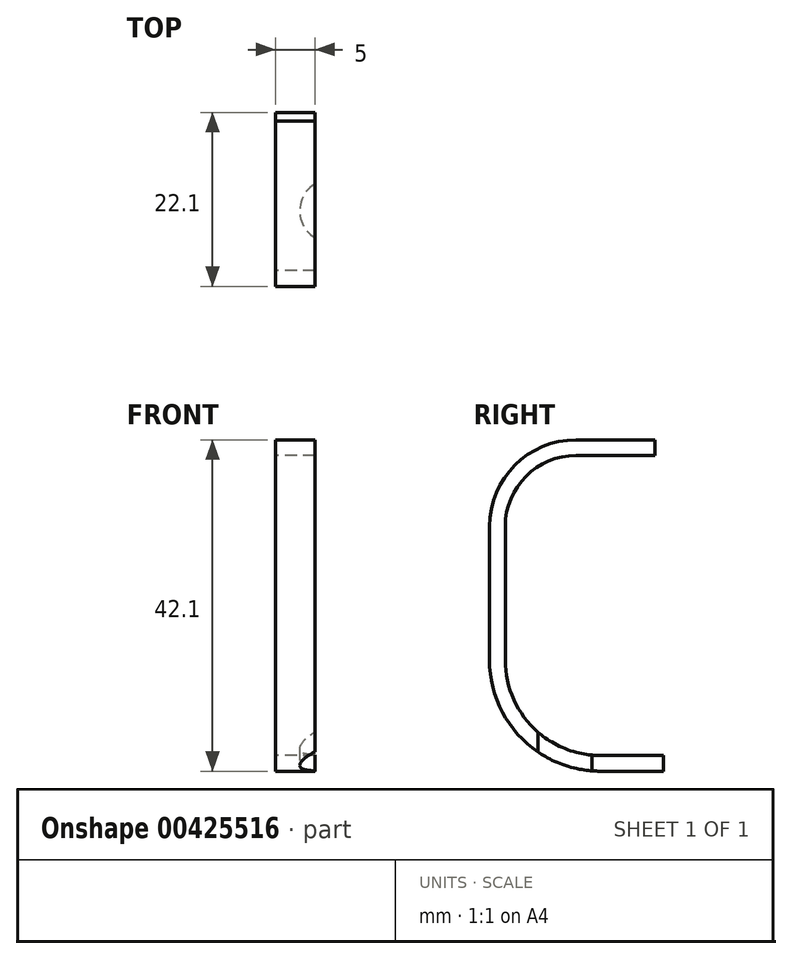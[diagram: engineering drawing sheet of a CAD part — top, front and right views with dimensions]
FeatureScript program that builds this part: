
annotation { "Feature Type Name" : "Feature", "Feature Type Description" : "" }
export const myFeature = defineFeature(function(context is Context, id is Id, definition is map)
    precondition{}
    {
        {
            var Q0;
            Q0=qCreatedBy(makeId("Right.planeOp"),FACE);
            var sketch = newSketch(context, id + "F0", { "sketchPlane" : qUnion([Q0])});
            skLineSegment(sketch, "E0", {"start": v(19, 9) * mm, "end": v(9, 9) * mm});
            skLineSegment(sketch, "E1", {"start": v(0, 0) * mm, "end": v(0, -17) * mm});
            skArc(sketch, "E2", {"start": v(9, 9) * mm, "mid": v(2.64, 6.36) * mm, "end": v(0, 0) * mm});
            skArc(sketch, "E3", {"start": v(0, -17) * mm, "mid": v(3.54, -25.56) * mm, "end": v(12.1, -29.1) * mm});
            skLineSegment(sketch, "E4.1", {"start": v(19, 11) * mm, "end": v(9, 11) * mm});
            skArc(sketch, "E4.2", {"start": v(9, 11) * mm, "mid": v(1.22, 7.78) * mm, "end": v(-2, 0) * mm});
            skLineSegment(sketch, "E4.3", {"start": v(-2, 0) * mm, "end": v(-2, -17) * mm});
            skArc(sketch, "E4.4", {"start": v(-2, -17) * mm, "mid": v(2.13, -26.97) * mm, "end": v(12.1, -31.1) * mm});
            skLineSegment(sketch, "E5", {"start": v(19, 11) * mm, "end": v(19, 9) * mm});
            skLineSegment(sketch, "E6", {"start": v(12.1, -29.1) * mm, "end": v(20.1, -29.1) * mm});
            skLineSegment(sketch, "E7", {"start": v(12.1, -31.1) * mm, "end": v(20.1, -31.1) * mm});
            skLineSegment(sketch, "E8", {"start": v(20.1, -29.1) * mm, "end": v(20.1, -31.1) * mm});
            skSolve(sketch);
        }
        {
            var Q0;
            Q0=makeQuery(id+"F0.imprint","IMPRINT",FACE,{"disambiguationData":[TD([[makeQuery(id+"F0.imprint","IMPRINT",EDGE,{"derivedFrom":sQuery(id+"F0.wireOp",EDGE,"E0")}),-1.0]])]});
            extrude(context, id + "F1", {"entities" : qUnion([Q0]), "depth" : 5 * mm});
        }
        {
            var Q0;
            Q0=makeQuery(id+"F1.opExtrude","SWEPT_FACE",FACE,{"disambiguationData":[OSD([sQuery(id+"F0.wireOp",EDGE,"E7")])]});
            var sketch = newSketch(context, id + "F2", { "sketchPlane" : qUnion([Q0])});
            skCircle(sketch, "E9", {"center": v(7.08, -7.6) * mm, "radius": 4 * mm});
            skSolve(sketch);
        }
        {
            var Q0;
            Q0=qSketchRegion(id+"F2",true);
            extrude(context, id + "F3", {"entities" : qUnion([Q0]), "operationType" : NewBodyOperationType.REMOVE, "oppositeDirection" : true, "depth" : 10 * mm});
        }
    });
